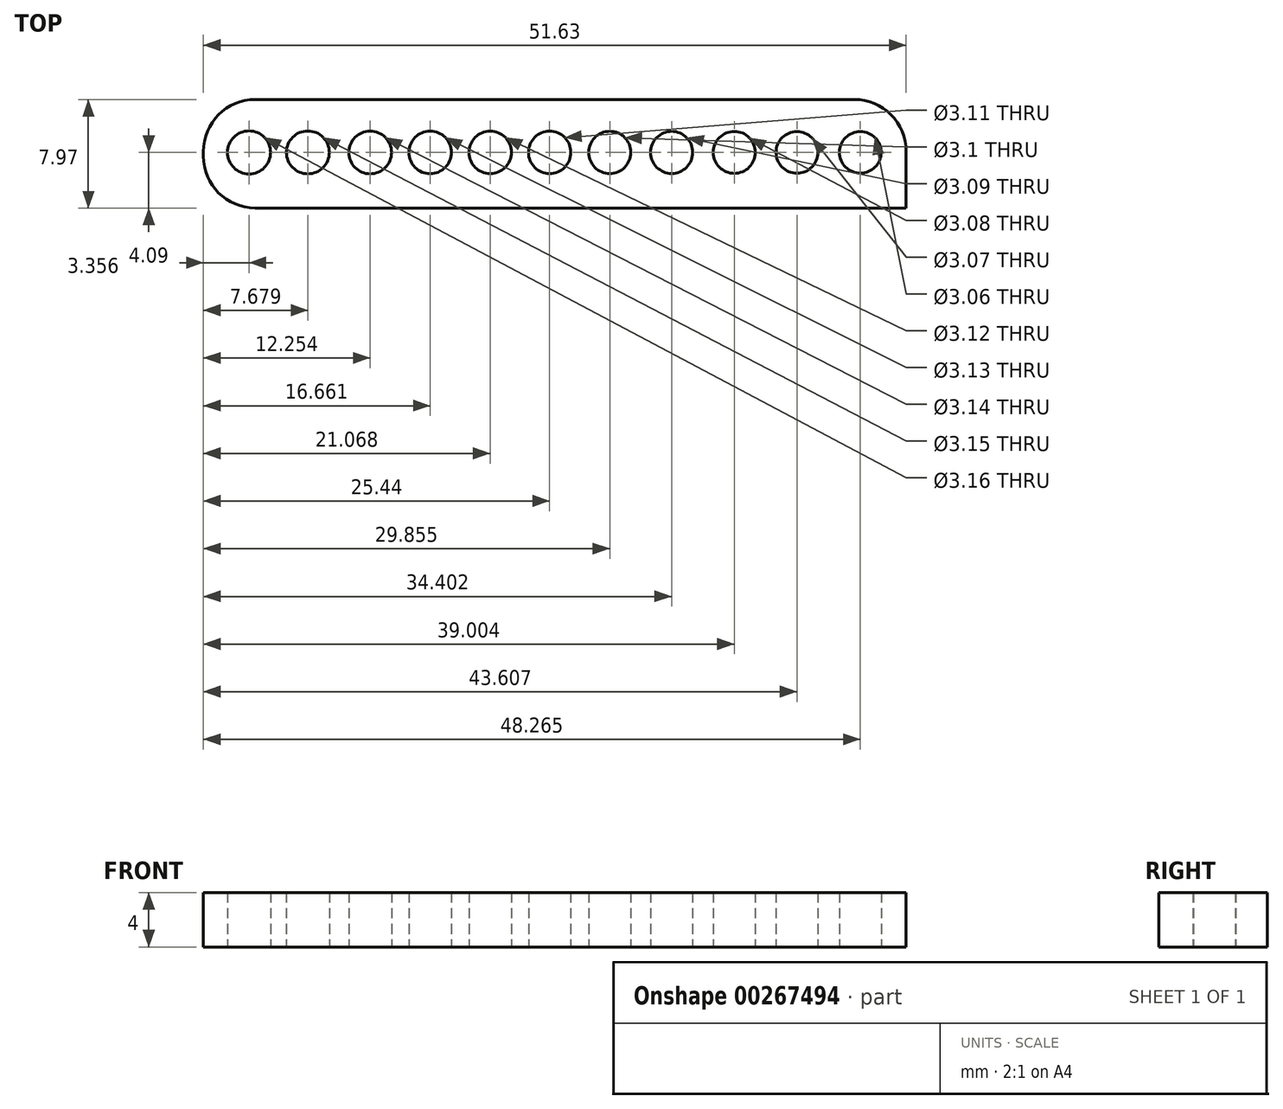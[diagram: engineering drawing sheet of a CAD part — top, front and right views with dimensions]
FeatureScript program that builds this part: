
annotation { "Feature Type Name" : "Feature", "Feature Type Description" : "" }
export const myFeature = defineFeature(function(context is Context, id is Id, definition is map)
    precondition{}
    {
        {
            var Q0;
            Q0=qCreatedBy(makeId("Top.planeOp"),FACE);
            var sketch = newSketch(context, id + "F0", { "sketchPlane" : qUnion([Q0])});
            skCircle(sketch, "E0", {"center": v(0, 0) * mm, "radius": 1.55 * mm});
            skCircle(sketch, "E1", {"center": v(4.41, 0) * mm, "radius": 1.55 * mm});
            skCircle(sketch, "E2", {"center": v(8.96, 0) * mm, "radius": 1.54 * mm});
            skCircle(sketch, "E3", {"center": v(13.56, 0) * mm, "radius": 1.54 * mm});
            skCircle(sketch, "E4", {"center": v(18.17, 0) * mm, "radius": 1.53 * mm});
            skCircle(sketch, "E5", {"center": v(22.82, 0) * mm, "radius": 1.53 * mm});
            skCircle(sketch, "E6", {"center": v(-4.37, 0) * mm, "radius": 1.56 * mm});
            skCircle(sketch, "E7", {"center": v(-8.78, 0) * mm, "radius": 1.56 * mm});
            skCircle(sketch, "E8", {"center": v(-13.19, 0) * mm, "radius": 1.57 * mm});
            skCircle(sketch, "E9", {"center": v(-17.76, 0) * mm, "radius": 1.57 * mm});
            skCircle(sketch, "E10", {"center": v(-22.08, 0) * mm, "radius": 1.58 * mm});
            skLineSegment(sketch, "E11.bottom", {"start": v(-21.63, 3.88) * mm, "end": v(22.38, 3.88) * mm});
            skLineSegment(sketch, "E11.top", {"start": v(-21.63, -4.09) * mm, "end": v(26.19, -4.09) * mm});
            skLineSegment(sketch, "E11.left", {"start": v(-25.44, 0.07) * mm, "end": v(-25.44, -0.28) * mm});
            skLineSegment(sketch, "E11.right", {"start": v(26.19, 0.07) * mm, "end": v(26.19, -4.09) * mm});
            skPoint(sketch, "E12.visualSharp", {"position": v(-25.44, 3.88) * mm});
            skArc(sketch, "E12.filletArc", {"start": v(-21.63, 3.88) * mm, "mid": v(-24.32, 2.77) * mm, "end": v(-25.44, 0.07) * mm});
            skPoint(sketch, "E13.visualSharp", {"position": v(-25.44, -4.09) * mm});
            skArc(sketch, "E13.filletArc", {"start": v(-25.44, -0.28) * mm, "mid": v(-24.32, -2.97) * mm, "end": v(-21.63, -4.09) * mm});
            skPoint(sketch, "E14.visualSharp", {"position": v(26.19, 3.88) * mm});
            skArc(sketch, "E14.filletArc", {"start": v(26.19, 0.07) * mm, "mid": v(25.07, 2.77) * mm, "end": v(22.38, 3.88) * mm});
            skSolve(sketch);
        }
        {
            var Q0;
            Q0=makeQuery(id+"F0.imprint","IMPRINT",FACE,{"disambiguationData":[TD([[makeQuery(id+"F0.imprint","IMPRINT",EDGE,{"derivedFrom":sQuery(id+"F0.wireOp",EDGE,"E0")}),-1.0]])]});
            extrude(context, id + "F1", {"entities" : qUnion([Q0]), "depth" : 4 * mm});
        }
    });
